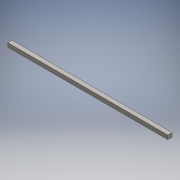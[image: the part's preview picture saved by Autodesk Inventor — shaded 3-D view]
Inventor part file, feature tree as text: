
AUTODESK INVENTOR PART (.ipt)
format: ipt  version: 2016 (Build 200138000, 138)  size: 109,056 bytes
history: native  units: mm
features: extrude x1, sketch x1
ambient origin geometry x8: Origin, YZ Plane, XZ Plane, XY Plane, X Axis, Y Axis, Z Axis, Center Point
bodies: Solid1 (feature_tree)
feature tree (2):
  extrude  "Extrusion1"  Depth=200.0mm
  sketch  "Sketch1"  dims[d0=7700.0mm d1=200.0mm d2=200.0mm d3=0.0mm]
